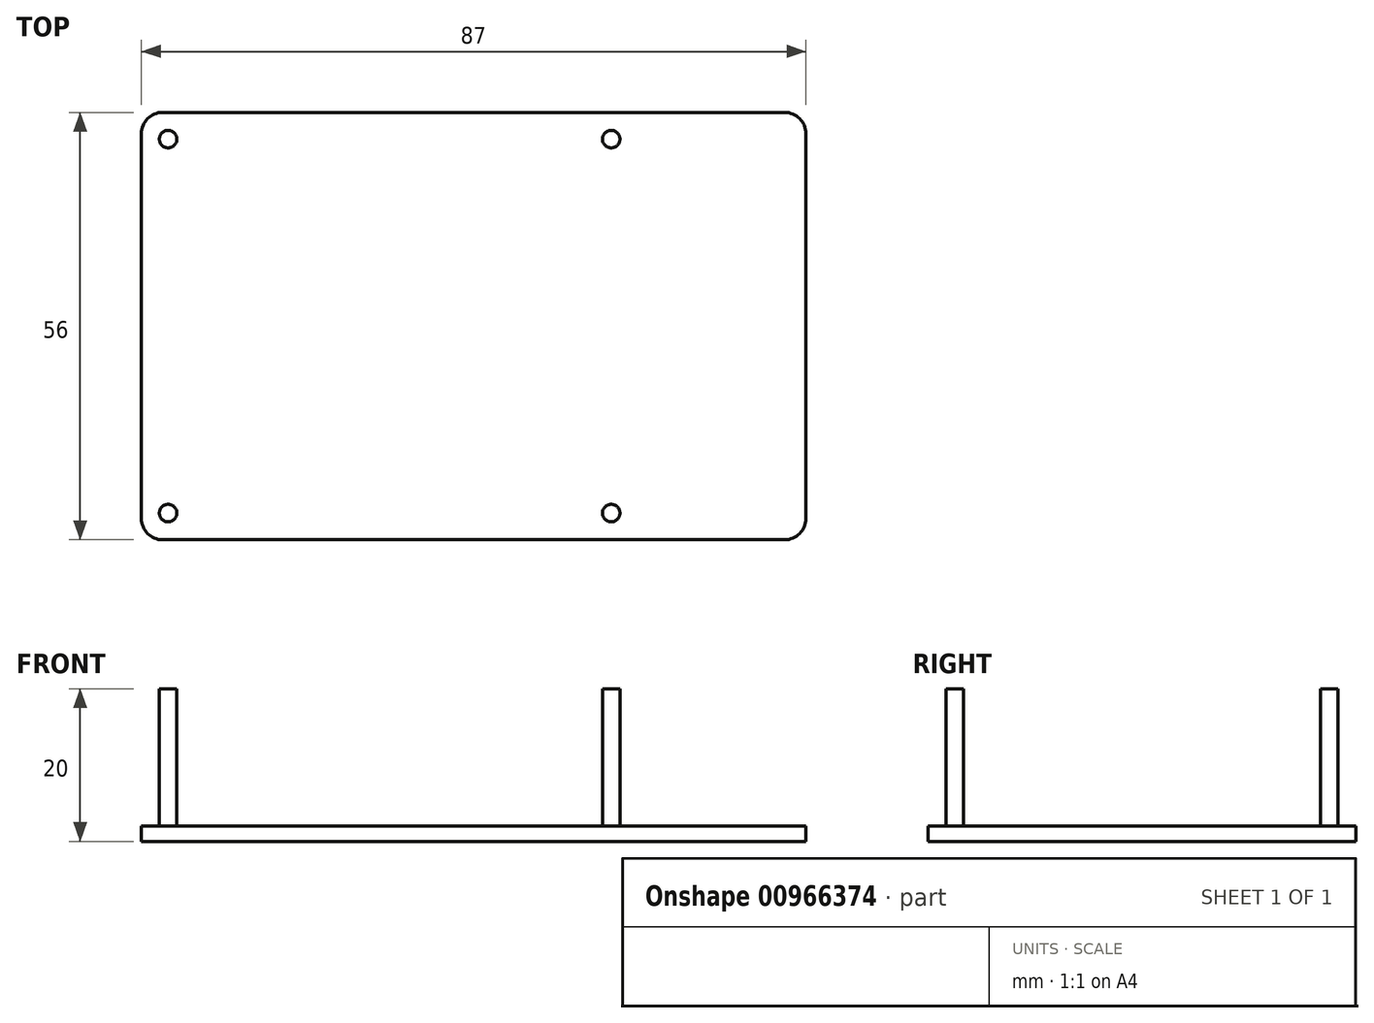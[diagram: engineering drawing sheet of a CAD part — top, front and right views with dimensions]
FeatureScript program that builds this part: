
annotation { "Feature Type Name" : "Feature", "Feature Type Description" : "" }
export const myFeature = defineFeature(function(context is Context, id is Id, definition is map)
    precondition{}
    {
        {
            var Q0;
            Q0=qCreatedBy(makeId("Top.planeOp"),FACE);
            var sketch = newSketch(context, id + "F0", { "sketchPlane" : qUnion([Q0])});
            skLineSegment(sketch, "E0.bottom", {"start": v(2.8, 0) * mm, "end": v(84.2, 0) * mm});
            skLineSegment(sketch, "E0.top", {"start": v(2.8, 56) * mm, "end": v(84.2, 56) * mm});
            skLineSegment(sketch, "E0.left", {"start": v(0, 2.8) * mm, "end": v(0, 53.2) * mm});
            skLineSegment(sketch, "E0.right", {"start": v(87, 2.8) * mm, "end": v(87, 53.2) * mm});
            skCircle(sketch, "E1", {"center": v(3.5, 3.5) * mm, "radius": 1.15 * mm});
            skCircle(sketch, "E2", {"center": v(3.5, 52.5) * mm, "radius": 1.15 * mm});
            skCircle(sketch, "E3", {"center": v(61.5, 52.5) * mm, "radius": 1.15 * mm});
            skCircle(sketch, "E4", {"center": v(61.5, 3.5) * mm, "radius": 1.15 * mm});
            skPoint(sketch, "E5.visualSharp", {"position": v(0, 0) * mm});
            skArc(sketch, "E5.filletArc", {"start": v(0, 2.8) * mm, "mid": v(0.82, 0.82) * mm, "end": v(2.8, 0) * mm});
            skPoint(sketch, "E6.visualSharp", {"position": v(87, 0) * mm});
            skArc(sketch, "E6.filletArc", {"start": v(84.2, 0) * mm, "mid": v(86.18, 0.82) * mm, "end": v(87, 2.8) * mm});
            skPoint(sketch, "E7.visualSharp", {"position": v(87, 56) * mm});
            skArc(sketch, "E7.filletArc", {"start": v(87, 53.2) * mm, "mid": v(86.18, 55.18) * mm, "end": v(84.2, 56) * mm});
            skPoint(sketch, "E8.visualSharp", {"position": v(0, 56) * mm});
            skArc(sketch, "E8.filletArc", {"start": v(2.8, 56) * mm, "mid": v(0.82, 55.18) * mm, "end": v(0, 53.2) * mm});
            skSolve(sketch);
        }
        {
            var Q0;
            Q0=makeQuery(id+"F0.imprint","IMPRINT",FACE,{"disambiguationData":[TD([[makeQuery(id+"F0.imprint","IMPRINT",EDGE,{"derivedFrom":sQuery(id+"F0.wireOp",EDGE,"E0.bottom")}),1.0]])]});
            var Q1;
            Q1=makeQuery(id+"F0.imprint","IMPRINT",FACE,{"disambiguationData":[TD([[makeQuery(id+"F0.imprint","IMPRINT",EDGE,{"derivedFrom":sQuery(id+"F0.wireOp",EDGE,"E1")}),1.0]])]});
            var Q2;
            Q2=makeQuery(id+"F0.imprint","IMPRINT",FACE,{"disambiguationData":[TD([[makeQuery(id+"F0.imprint","IMPRINT",EDGE,{"derivedFrom":sQuery(id+"F0.wireOp",EDGE,"E3")}),1.0]])]});
            var Q3;
            Q3=makeQuery(id+"F0.imprint","IMPRINT",FACE,{"disambiguationData":[TD([[makeQuery(id+"F0.imprint","IMPRINT",EDGE,{"derivedFrom":sQuery(id+"F0.wireOp",EDGE,"E4")}),1.0]])]});
            var Q4;
            Q4=makeQuery(id+"F0.imprint","IMPRINT",FACE,{"disambiguationData":[TD([[makeQuery(id+"F0.imprint","IMPRINT",EDGE,{"derivedFrom":sQuery(id+"F0.wireOp",EDGE,"E3")}),1.0]])]});
            var Q5;
            Q5=makeQuery(id+"F0.imprint","IMPRINT",FACE,{"disambiguationData":[TD([[makeQuery(id+"F0.imprint","IMPRINT",EDGE,{"derivedFrom":sQuery(id+"F0.wireOp",EDGE,"E4")}),1.0]])]});
            var Q6;
            Q6=makeQuery(id+"F0.imprint","IMPRINT",FACE,{"disambiguationData":[TD([[makeQuery(id+"F0.imprint","IMPRINT",EDGE,{"derivedFrom":sQuery(id+"F0.wireOp",EDGE,"E2")}),1.0]])]});
            extrude(context, id + "F1", {"entities" : qUnion([Q0, Q1, Q2, Q3, Q4, Q5, Q6]), "depth" : 2 * mm, "offsetDistance" : 25 * mm});
        }
        {
            var Q0;
            Q0=makeQuery(id+"F0.imprint","IMPRINT",FACE,{"disambiguationData":[TD([[makeQuery(id+"F0.imprint","IMPRINT",EDGE,{"derivedFrom":sQuery(id+"F0.wireOp",EDGE,"E4")}),1.0]])]});
            var Q1;
            Q1=makeQuery(id+"F0.imprint","IMPRINT",FACE,{"disambiguationData":[TD([[makeQuery(id+"F0.imprint","IMPRINT",EDGE,{"derivedFrom":sQuery(id+"F0.wireOp",EDGE,"E3")}),1.0]])]});
            var Q2;
            Q2=makeQuery(id+"F0.imprint","IMPRINT",FACE,{"disambiguationData":[TD([[makeQuery(id+"F0.imprint","IMPRINT",EDGE,{"derivedFrom":sQuery(id+"F0.wireOp",EDGE,"E2")}),1.0]])]});
            var Q3;
            Q3=makeQuery(id+"F0.imprint","IMPRINT",FACE,{"disambiguationData":[TD([[makeQuery(id+"F0.imprint","IMPRINT",EDGE,{"derivedFrom":sQuery(id+"F0.wireOp",EDGE,"E1")}),1.0]])]});
            extrude(context, id + "F2", {"entities" : qUnion([Q0, Q1, Q2, Q3]), "operationType" : NewBodyOperationType.ADD, "depth" : 105 * mm, "offsetDistance" : 25 * mm});
        }
        {
            var Q0;
            Q0=qCreatedBy(makeId("Top.planeOp"),FACE);
            cPlane(context, id + "F3", {"entities" : qUnion([Q0]), "cplaneType" : CPlaneType.OFFSET, "offset" : 25 * mm, "width" : 150 * mm, "height" : 150 * mm});
        }
        {
            var Q0;
            Q0=qCreatedBy(id+"F3.planeOp",FACE);
            var sketch = newSketch(context, id + "F4", { "sketchPlane" : qUnion([Q0])});
            skPoint(sketch, "E9.0", {"position": v(3.5, 52.5) * mm});
            skPoint(sketch, "E10.0", {"position": v(61.5, 52.5) * mm});
            skPoint(sketch, "E11.0", {"position": v(3.5, 3.5) * mm});
            skPoint(sketch, "E12.0", {"position": v(61.5, 3.5) * mm});
            skLineSegment(sketch, "E13.0", {"start": v(2.8, 56) * mm, "end": v(84.2, 56) * mm});
            skPoint(sketch, "E14.0", {"position": v(0.82, 55.18) * mm});
            skLineSegment(sketch, "E15.0", {"start": v(0, 2.8) * mm, "end": v(0, 53.2) * mm});
            skArc(sketch, "E16.0", {"start": v(2.8, 56) * mm, "mid": v(0.82, 55.18) * mm, "end": v(0, 53.2) * mm});
            skArc(sketch, "E17.0", {"start": v(87, 53.2) * mm, "mid": v(86.18, 55.18) * mm, "end": v(84.2, 56) * mm});
            skLineSegment(sketch, "E18.0", {"start": v(87, 2.8) * mm, "end": v(87, 53.2) * mm});
            skLineSegment(sketch, "E19.0", {"start": v(2.8, 0) * mm, "end": v(84.2, 0) * mm});
            skArc(sketch, "E20.0", {"start": v(84.2, 0) * mm, "mid": v(86.18, 0.82) * mm, "end": v(87, 2.8) * mm});
            skArc(sketch, "E21.0", {"start": v(0, 2.8) * mm, "mid": v(0.82, 0.82) * mm, "end": v(2.8, 0) * mm});
            skCircle(sketch, "E22", {"center": v(3.5, 52.5) * mm, "radius": 1.75 * mm});
            skCircle(sketch, "E23", {"center": v(3.5, 3.5) * mm, "radius": 1.75 * mm});
            skCircle(sketch, "E24", {"center": v(61.5, 3.5) * mm, "radius": 1.75 * mm});
            skCircle(sketch, "E25", {"center": v(61.5, 52.5) * mm, "radius": 1.75 * mm});
            skCircle(sketch, "E26", {"center": v(3.5, 3.5) * mm, "radius": 2.75 * mm});
            skCircle(sketch, "E27", {"center": v(61.5, 3.5) * mm, "radius": 2.75 * mm});
            skCircle(sketch, "E28", {"center": v(3.5, 52.5) * mm, "radius": 2.75 * mm});
            skCircle(sketch, "E29", {"center": v(61.5, 52.5) * mm, "radius": 2.75 * mm});
            skSolve(sketch);
        }
        {
            var Q0;
            Q0=makeQuery(id+"F4.imprint","IMPRINT",FACE,{"disambiguationData":[TD([[makeQuery(id+"F4.imprint","IMPRINT",EDGE,{"derivedFrom":sQuery(id+"F4.wireOp",EDGE,"E23")}),1.0]])]});
            var Q1;
            Q1=makeQuery(id+"F4.imprint","IMPRINT",FACE,{"disambiguationData":[TD([[makeQuery(id+"F4.imprint","IMPRINT",EDGE,{"derivedFrom":sQuery(id+"F4.wireOp",EDGE,"E23")}),-1.0]])]});
            var Q2;
            Q2=makeQuery(id+"F4.imprint","IMPRINT",FACE,{"disambiguationData":[TD([[makeQuery(id+"F4.imprint","IMPRINT",EDGE,{"derivedFrom":sQuery(id+"F4.wireOp",EDGE,"E13.0")}),-1.0]])]});
            var Q3;
            Q3=makeQuery(id+"F4.imprint","IMPRINT",FACE,{"disambiguationData":[TD([[makeQuery(id+"F4.imprint","IMPRINT",EDGE,{"derivedFrom":sQuery(id+"F4.wireOp",EDGE,"E24")}),-1.0]])]});
            var Q4;
            Q4=makeQuery(id+"F4.imprint","IMPRINT",FACE,{"disambiguationData":[TD([[makeQuery(id+"F4.imprint","IMPRINT",EDGE,{"derivedFrom":sQuery(id+"F4.wireOp",EDGE,"E24")}),1.0]])]});
            var Q5;
            Q5=makeQuery(id+"F4.imprint","IMPRINT",FACE,{"disambiguationData":[TD([[makeQuery(id+"F4.imprint","IMPRINT",EDGE,{"derivedFrom":sQuery(id+"F4.wireOp",EDGE,"E25")}),-1.0]])]});
            var Q6;
            Q6=makeQuery(id+"F4.imprint","IMPRINT",FACE,{"disambiguationData":[TD([[makeQuery(id+"F4.imprint","IMPRINT",EDGE,{"derivedFrom":sQuery(id+"F4.wireOp",EDGE,"E25")}),1.0]])]});
            var Q7;
            Q7=makeQuery(id+"F4.imprint","IMPRINT",FACE,{"disambiguationData":[TD([[makeQuery(id+"F4.imprint","IMPRINT",EDGE,{"derivedFrom":sQuery(id+"F4.wireOp",EDGE,"E22")}),-1.0]])]});
            var Q8;
            Q8=makeQuery(id+"F4.imprint","IMPRINT",FACE,{"disambiguationData":[TD([[makeQuery(id+"F4.imprint","IMPRINT",EDGE,{"derivedFrom":sQuery(id+"F4.wireOp",EDGE,"E22")}),1.0]])]});
            extrude(context, id + "F5", {"entities" : qUnion([Q0, Q1, Q2, Q3, Q4, Q5, Q6, Q7, Q8]), "depth" : 2 * mm, "offsetDistance" : 25 * mm});
        }
        {
            var Q0;
            Q0=makeQuery(id+"F4.imprint","IMPRINT",FACE,{"disambiguationData":[TD([[makeQuery(id+"F4.imprint","IMPRINT",EDGE,{"derivedFrom":sQuery(id+"F4.wireOp",EDGE,"E23")}),-1.0]])]});
            var Q1;
            Q1=makeQuery(id+"F4.imprint","IMPRINT",FACE,{"disambiguationData":[TD([[makeQuery(id+"F4.imprint","IMPRINT",EDGE,{"derivedFrom":sQuery(id+"F4.wireOp",EDGE,"E22")}),-1.0]])]});
            var Q2;
            Q2=makeQuery(id+"F4.imprint","IMPRINT",FACE,{"disambiguationData":[TD([[makeQuery(id+"F4.imprint","IMPRINT",EDGE,{"derivedFrom":sQuery(id+"F4.wireOp",EDGE,"E25")}),-1.0]])]});
            var Q3;
            Q3=makeQuery(id+"F4.imprint","IMPRINT",FACE,{"disambiguationData":[TD([[makeQuery(id+"F4.imprint","IMPRINT",EDGE,{"derivedFrom":sQuery(id+"F4.wireOp",EDGE,"E24")}),-1.0]])]});
            var Q4;
            Q4=makeQuery(id+"F5.opExtrude","CAP_FACE",FACE,{"disambiguationData":[OSD([sQuery(id+"F4.wireOp",EDGE,"E13.0"),sQuery(id+"F4.wireOp",EDGE,"E15.0"),sQuery(id+"F4.wireOp",EDGE,"E16.0"),sQuery(id+"F4.wireOp",EDGE,"E17.0"),sQuery(id+"F4.wireOp",EDGE,"E18.0"),sQuery(id+"F4.wireOp",EDGE,"E19.0"),sQuery(id+"F4.wireOp",EDGE,"E20.0"),sQuery(id+"F4.wireOp",EDGE,"E21.0"),sQuery(id+"F4.wireOp",EDGE,"E26"),sQuery(id+"F4.wireOp",EDGE,"E27"),sQuery(id+"F4.wireOp",EDGE,"E28"),sQuery(id+"F4.wireOp",EDGE,"E29")])],"isStart":false});
            var Q5;
            Q5=makeQuery(id+"F5.opExtrude","SWEPT_BODY",BODY,{"disambiguationData":[OSD([sQuery(id+"F4.wireOp",EDGE,"E13.0"),sQuery(id+"F4.wireOp",EDGE,"E15.0"),sQuery(id+"F4.wireOp",EDGE,"E16.0"),sQuery(id+"F4.wireOp",EDGE,"E17.0"),sQuery(id+"F4.wireOp",EDGE,"E18.0"),sQuery(id+"F4.wireOp",EDGE,"E19.0"),sQuery(id+"F4.wireOp",EDGE,"E20.0"),sQuery(id+"F4.wireOp",EDGE,"E21.0"),sQuery(id+"F4.wireOp",EDGE,"E26"),sQuery(id+"F4.wireOp",EDGE,"E27"),sQuery(id+"F4.wireOp",EDGE,"E28"),sQuery(id+"F4.wireOp",EDGE,"E29")])]});
            extrude(context, id + "F6", {"entities" : qUnion([Q0, Q1, Q2, Q3]), "operationType" : NewBodyOperationType.ADD, "endBound" : BoundingType.UP_TO_SURFACE, "depth" : 20 * mm, "endBoundEntityFace" : qUnion([Q4]), "endBoundEntityBody" : qUnion([Q5]), "offsetDistance" : 25 * mm});
        }
        {
            var Q0;
            Q0=makeQuery(id+"F1.opExtrude","SWEPT_BODY",BODY,{"disambiguationData":[OSD([sQuery(id+"F0.wireOp",EDGE,"E0.bottom"),sQuery(id+"F0.wireOp",EDGE,"E0.top"),sQuery(id+"F0.wireOp",EDGE,"E0.left"),sQuery(id+"F0.wireOp",EDGE,"E0.right"),sQuery(id+"F0.wireOp",EDGE,"E5.filletArc"),sQuery(id+"F0.wireOp",EDGE,"E6.filletArc"),sQuery(id+"F0.wireOp",EDGE,"E7.filletArc"),sQuery(id+"F0.wireOp",EDGE,"E8.filletArc")])]});
            deleteBodies(context, id + "F7", {"entities" : qUnion([Q0])});
        }
        {
            var Q0;
            Q0=makeQuery(id+"F5.opExtrude","CAP_FACE",FACE,{"disambiguationData":[OSD([sQuery(id+"F4.wireOp",EDGE,"E13.0"),sQuery(id+"F4.wireOp",EDGE,"E15.0"),sQuery(id+"F4.wireOp",EDGE,"E16.0"),sQuery(id+"F4.wireOp",EDGE,"E17.0"),sQuery(id+"F4.wireOp",EDGE,"E18.0"),sQuery(id+"F4.wireOp",EDGE,"E19.0"),sQuery(id+"F4.wireOp",EDGE,"E20.0"),sQuery(id+"F4.wireOp",EDGE,"E21.0")])],"isStart":false});
            var sketch = newSketch(context, id + "F8", { "sketchPlane" : qUnion([Q0])});
            skCircle(sketch, "E30.0", {"center": v(3.5, 52.5) * mm, "radius": 1.15 * mm});
            skCircle(sketch, "E31.0", {"center": v(61.5, 52.5) * mm, "radius": 1.15 * mm});
            skCircle(sketch, "E32.0", {"center": v(61.5, 3.5) * mm, "radius": 1.15 * mm});
            skCircle(sketch, "E33.0", {"center": v(3.5, 3.5) * mm, "radius": 1.15 * mm});
            skSolve(sketch);
        }
        {
            var Q0;
            Q0=qSketchRegion(id+"F8",true);
            extrude(context, id + "F9", {"entities" : qUnion([Q0]), "operationType" : NewBodyOperationType.ADD, "depth" : 18 * mm, "offsetDistance" : 25 * mm});
        }
    });
